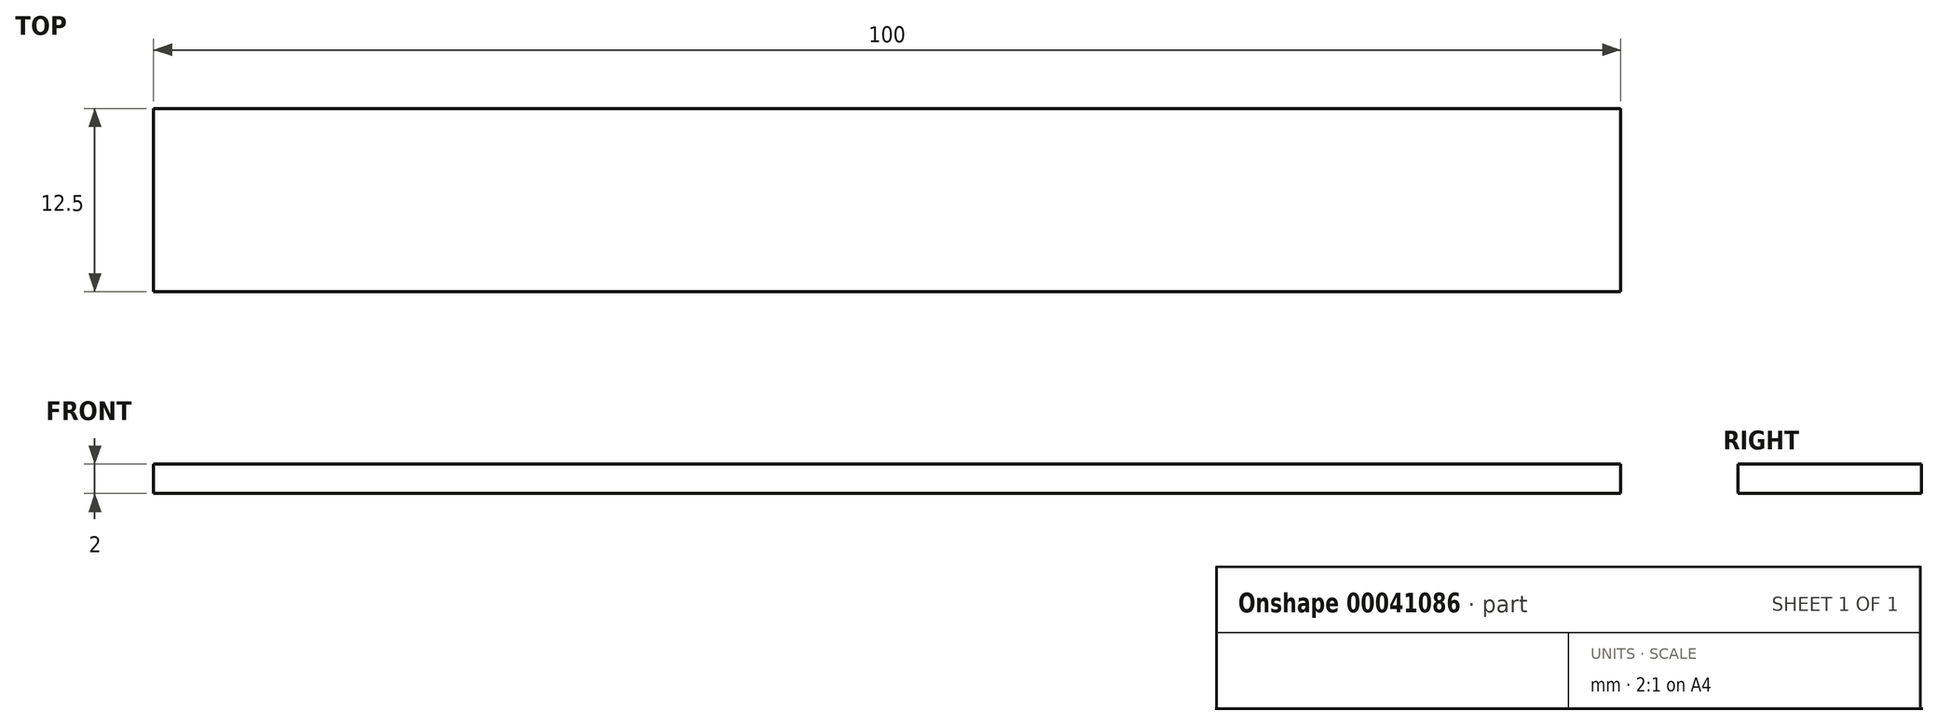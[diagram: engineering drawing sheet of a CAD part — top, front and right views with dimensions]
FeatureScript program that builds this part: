
annotation { "Feature Type Name" : "Feature", "Feature Type Description" : "" }
export const myFeature = defineFeature(function(context is Context, id is Id, definition is map)
    precondition{}
    {
        {
            var Q0;
            Q0=qCreatedBy(makeId("Top.planeOp"),FACE);
            var sketch = newSketch(context, id + "F0", { "sketchPlane" : qUnion([Q0])});
            skLineSegment(sketch, "E0.bottom", {"start": v(0, 0) * mm, "end": v(100, 0) * mm});
            skLineSegment(sketch, "E0.top", {"start": v(0, 12.5) * mm, "end": v(100, 12.5) * mm});
            skLineSegment(sketch, "E0.left", {"start": v(0, 0) * mm, "end": v(0, 12.5) * mm});
            skLineSegment(sketch, "E0.right", {"start": v(100, 0) * mm, "end": v(100, 12.5) * mm});
            skSolve(sketch);
        }
        {
            var Q0;
            Q0 = qSketchRegion(id + "F0", true);
            extrude(context, id + "F1", {"entities" : qUnion([Q0]), "depth" : 2 * mm});
        }
    });
